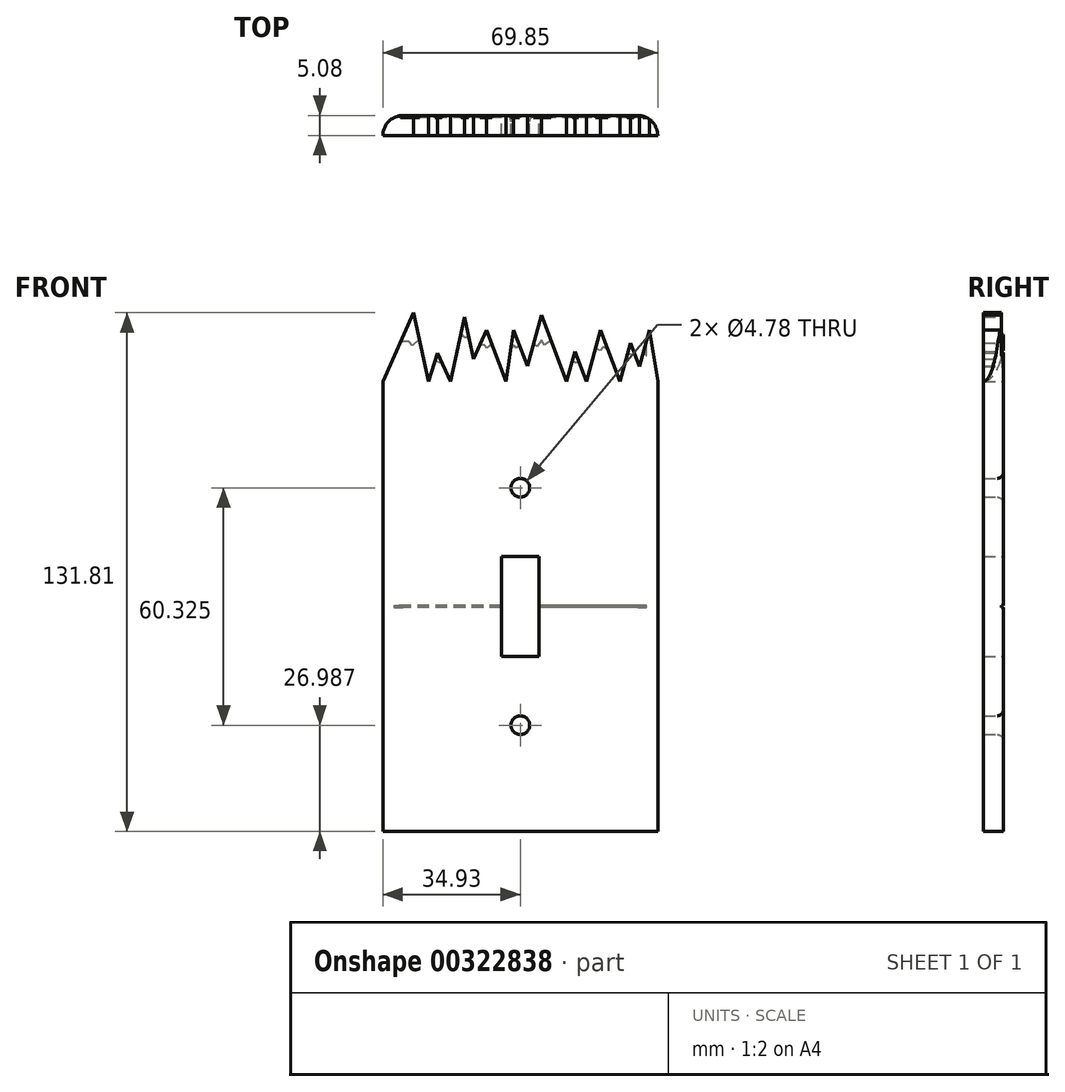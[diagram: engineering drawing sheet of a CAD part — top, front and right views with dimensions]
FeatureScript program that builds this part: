
annotation { "Feature Type Name" : "Feature", "Feature Type Description" : "" }
export const myFeature = defineFeature(function(context is Context, id is Id, definition is map)
    precondition{}
    {
        {
            var Q0;
            Q0=qCreatedBy(makeId("Front.planeOp"),FACE);
            var sketch = newSketch(context, id + "F0", { "sketchPlane" : qUnion([Q0])});
            skLineSegment(sketch, "E0.bottom", {"start": v(34.92, 57.15) * mm, "end": v(-34.93, 57.15) * mm});
            skLineSegment(sketch, "E0.top", {"start": v(34.93, -57.15) * mm, "end": v(-34.92, -57.15) * mm});
            skLineSegment(sketch, "E0.left", {"start": v(34.92, 57.15) * mm, "end": v(34.93, -57.15) * mm});
            skLineSegment(sketch, "E0.right", {"start": v(-34.93, 57.15) * mm, "end": v(-34.92, -57.15) * mm});
            skPoint(sketch, "E0.middle", {"position": v(0, 0) * mm});
            skLineSegment(sketch, "E1.bottom", {"start": v(4.76, 12.7) * mm, "end": v(-4.76, 12.7) * mm});
            skLineSegment(sketch, "E1.top", {"start": v(4.76, -12.7) * mm, "end": v(-4.76, -12.7) * mm});
            skLineSegment(sketch, "E1.left", {"start": v(4.76, 12.7) * mm, "end": v(4.76, -12.7) * mm});
            skLineSegment(sketch, "E1.right", {"start": v(-4.76, 12.7) * mm, "end": v(-4.76, -12.7) * mm});
            skCircle(sketch, "E2", {"center": v(0, 30.16) * mm, "radius": 2.39 * mm});
            skCircle(sketch, "E3", {"center": v(0, -30.16) * mm, "radius": 2.39 * mm});
            skSolve(sketch);
        }
        {
            var Q0;
            Q0=makeQuery(id+"F0.imprint","IMPRINT",FACE,{"disambiguationData":[TD([[makeQuery(id+"F0.imprint","IMPRINT",EDGE,{"derivedFrom":sQuery(id+"F0.wireOp",EDGE,"E0.bottom")}),1.0]])]});
            var sketch = newSketch(context, id + "F1", { "sketchPlane" : qUnion([Q0])});
            skSolve(sketch);
        }
        {
            var Q0;
            Q0=makeQuery(id+"F1.imprint","IMPRINT",FACE,{"disambiguationData":[TD([[makeQuery(id+"F1.imprint","IMPRINT",EDGE,{"derivedFrom":makeQuery(id+"F0.imprint","IMPRINT",EDGE,{"derivedFrom":sQuery(id+"F0.wireOp",EDGE,"E0.bottom")})}),1.0]])]});
            var sketch = newSketch(context, id + "F2", { "sketchPlane" : qUnion([Q0])});
            skLineSegment(sketch, "E4.0.0", {"start": v(-34.92, -57.15) * mm, "end": v(34.93, -57.15) * mm});
            skLineSegment(sketch, "E4.0.1", {"start": v(34.93, -57.15) * mm, "end": v(34.92, 57.15) * mm});
            skLineSegment(sketch, "E4.0.2", {"start": v(34.92, 57.15) * mm, "end": v(-34.93, 57.15) * mm});
            skLineSegment(sketch, "E4.0.3", {"start": v(-34.93, 57.15) * mm, "end": v(-34.92, -57.15) * mm});
            skLineSegment(sketch, "E5", {"start": v(-34.93, 57.15) * mm, "end": v(-27.12, 74.66) * mm});
            skLineSegment(sketch, "E6", {"start": v(-27.12, 74.66) * mm, "end": v(-23.3, 57.15) * mm});
            skLineSegment(sketch, "E7", {"start": v(-23.3, 57.15) * mm, "end": v(-21, 64.35) * mm});
            skLineSegment(sketch, "E8", {"start": v(-21, 64.35) * mm, "end": v(-17.76, 57.15) * mm});
            skLineSegment(sketch, "E9", {"start": v(-17.76, 57.15) * mm, "end": v(-14.13, 73.52) * mm});
            skLineSegment(sketch, "E10", {"start": v(-14.13, 73.52) * mm, "end": v(-11.84, 62.82) * mm});
            skLineSegment(sketch, "E11", {"start": v(-11.84, 62.82) * mm, "end": v(-8.6, 70.27) * mm});
            skLineSegment(sketch, "E12", {"start": v(-8.6, 70.27) * mm, "end": v(-3.63, 57.15) * mm});
            skLineSegment(sketch, "E13", {"start": v(-3.63, 57.15) * mm, "end": v(-1.72, 70.27) * mm});
            skLineSegment(sketch, "E14", {"start": v(-1.72, 70.27) * mm, "end": v(1.77, 61.05) * mm});
            skLineSegment(sketch, "E15", {"start": v(1.77, 61.05) * mm, "end": v(5.35, 74.1) * mm});
            skLineSegment(sketch, "E16", {"start": v(5.35, 74.1) * mm, "end": v(11.76, 57.15) * mm});
            skLineSegment(sketch, "E17", {"start": v(11.76, 57.15) * mm, "end": v(13.86, 64.8) * mm});
            skLineSegment(sketch, "E18", {"start": v(13.86, 64.8) * mm, "end": v(16.76, 57.15) * mm});
            skLineSegment(sketch, "E19", {"start": v(16.76, 57.15) * mm, "end": v(20.36, 70.27) * mm});
            skLineSegment(sketch, "E20", {"start": v(20.36, 70.27) * mm, "end": v(25.32, 57.15) * mm});
            skLineSegment(sketch, "E21", {"start": v(25.32, 57.15) * mm, "end": v(27.99, 66.87) * mm});
            skLineSegment(sketch, "E22", {"start": v(27.99, 66.87) * mm, "end": v(30.22, 60.98) * mm});
            skLineSegment(sketch, "E23", {"start": v(30.22, 60.98) * mm, "end": v(32.77, 70.27) * mm});
            skLineSegment(sketch, "E24", {"start": v(32.77, 70.27) * mm, "end": v(34.92, 57.15) * mm});
            skLineSegment(sketch, "E25", {"start": v(-29.32, 69.72) * mm, "end": v(-28.13, 67.6) * mm});
            skLineSegment(sketch, "E26", {"start": v(-28.13, 67.6) * mm, "end": v(-27.43, 69.16) * mm});
            skLineSegment(sketch, "E27", {"start": v(-27.43, 69.16) * mm, "end": v(-25.61, 67.76) * mm});
            skLineSegment(sketch, "E28", {"start": v(-22.15, 60.75) * mm, "end": v(-19.85, 61.79) * mm});
            skLineSegment(sketch, "E29", {"start": v(-15.51, 67.28) * mm, "end": v(-13.9, 64.92) * mm});
            skLineSegment(sketch, "E30", {"start": v(-13.9, 64.92) * mm, "end": v(-12.71, 66.9) * mm});
            skLineSegment(sketch, "E31", {"start": v(-10.4, 66.1) * mm, "end": v(-8.65, 63.97) * mm});
            skPoint(sketch, "E31.startSnap0", {"position": v(-14.7, 66.1) * mm});
            skLineSegment(sketch, "E32", {"start": v(-8.65, 63.97) * mm, "end": v(-8.08, 65.28) * mm});
            skLineSegment(sketch, "E33", {"start": v(-8.08, 65.28) * mm, "end": v(-6.43, 64.56) * mm});
            skLineSegment(sketch, "E34", {"start": v(-2.48, 65.04) * mm, "end": v(0.03, 65.98) * mm});
            skPoint(sketch, "E34.endSnap0", {"position": v(0.03, 65.66) * mm});
            skLineSegment(sketch, "E35", {"start": v(3.56, 67.57) * mm, "end": v(4.52, 65.04) * mm});
            skLineSegment(sketch, "E36", {"start": v(4.52, 65.04) * mm, "end": v(5.15, 67.35) * mm});
            skLineSegment(sketch, "E37", {"start": v(5.15, 67.35) * mm, "end": v(6.72, 65.04) * mm});
            skLineSegment(sketch, "E38", {"start": v(6.72, 65.04) * mm, "end": v(8.35, 66.14) * mm});
            skLineSegment(sketch, "E39", {"start": v(18.9, 64.96) * mm, "end": v(19.75, 62.72) * mm});
            skLineSegment(sketch, "E40", {"start": v(19.75, 62.72) * mm, "end": v(21.14, 64.25) * mm});
            skLineSegment(sketch, "E41", {"start": v(21.14, 64.25) * mm, "end": v(23.05, 63.16) * mm});
            skLineSegment(sketch, "E42", {"start": v(26.88, 62.84) * mm, "end": v(27.52, 61.17) * mm});
            skLineSegment(sketch, "E43", {"start": v(27.52, 61.17) * mm, "end": v(27.86, 62.44) * mm});
            skLineSegment(sketch, "E44", {"start": v(27.86, 62.44) * mm, "end": v(29.87, 61.89) * mm});
            skLineSegment(sketch, "E45", {"start": v(31.5, 65.63) * mm, "end": v(33.63, 65.04) * mm});
            skSolve(sketch);
        }
        {
            var Q0;
            Q0=makeQuery(id+"F1.imprint","IMPRINT",FACE,{"disambiguationData":[TD([[makeQuery(id+"F1.imprint","IMPRINT",EDGE,{"derivedFrom":makeQuery(id+"F0.imprint","IMPRINT",EDGE,{"derivedFrom":sQuery(id+"F0.wireOp",EDGE,"E0.bottom")})}),1.0]])]});
            extrude(context, id + "F3", {"entities" : qUnion([Q0]), "depth" : 5.08 * mm});
        }
        {
            var Q0;
            {var subQ0=sQuery(id+"F2.wireOp",EDGE,"E39");Q0=makeQuery(id+"F2.imprint","IMPRINT",FACE,{"disambiguationData":[TD([[makeQuery(id+"F2.imprint","IMPRINT",EDGE,{"derivedFrom":subQ0}),-1.0]])]});}
            var Q1;
            {var subQ4=sQuery(id+"F2.wireOp",EDGE,"E39");Q1=makeQuery(id+"F2.imprint","IMPRINT",FACE,{"disambiguationData":[TD([[makeQuery(id+"F2.imprint","IMPRINT",EDGE,{"derivedFrom":subQ4}),1.0]])]});}
            var Q2;
            {var subQ10=sQuery(id+"F2.wireOp",EDGE,"E42");Q2=makeQuery(id+"F2.imprint","IMPRINT",FACE,{"disambiguationData":[TD([[makeQuery(id+"F2.imprint","IMPRINT",EDGE,{"derivedFrom":subQ10}),-1.0]])]});}
            var Q3;
            {var subQ0=sQuery(id+"F2.wireOp",EDGE,"E42");Q3=makeQuery(id+"F2.imprint","IMPRINT",FACE,{"disambiguationData":[TD([[makeQuery(id+"F2.imprint","IMPRINT",EDGE,{"derivedFrom":subQ0}),1.0]])]});}
            var Q4;
            {var subQ3=sQuery(id+"F2.wireOp",EDGE,"E45");Q4=makeQuery(id+"F2.imprint","IMPRINT",FACE,{"disambiguationData":[TD([[makeQuery(id+"F2.imprint","IMPRINT",EDGE,{"derivedFrom":subQ3}),1.0]])]});}
            var Q5;
            {var subQ0=sQuery(id+"F2.wireOp",EDGE,"E17");Q5=makeQuery(id+"F2.imprint","IMPRINT",FACE,{"disambiguationData":[TD([[makeQuery(id+"F2.imprint","IMPRINT",EDGE,{"derivedFrom":subQ0}),-1.0]])]});}
            var Q6;
            {var subQ7=sQuery(id+"F2.wireOp",EDGE,"E35");Q6=makeQuery(id+"F2.imprint","IMPRINT",FACE,{"disambiguationData":[TD([[makeQuery(id+"F2.imprint","IMPRINT",EDGE,{"derivedFrom":subQ7}),-1.0]])]});}
            var Q7;
            {var subQ0=sQuery(id+"F2.wireOp",EDGE,"E35");Q7=makeQuery(id+"F2.imprint","IMPRINT",FACE,{"disambiguationData":[TD([[makeQuery(id+"F2.imprint","IMPRINT",EDGE,{"derivedFrom":subQ0}),1.0]])]});}
            var Q8;
            {var subQ0=sQuery(id+"F2.wireOp",EDGE,"E14");var subQ1=sQuery(id+"F2.wireOp",EDGE,"E13");var subQ2=makeQuery(id+"F2.imprint","INTERSECT",VERTEX,{"derivedFrom":[subQ1,subQ0]});Q8=makeQuery(id+"F2.imprint","IMPRINT",FACE,{"disambiguationData":[TD([[makeQuery(id+"F2.imprint","IMPRINT",EDGE,{"disambiguationData":[TD([[subQ2,1.0]])],"derivedFrom":subQ1}),-1.0]])]});}
            var Q9;
            {var subQ11=sQuery(id+"F2.wireOp",EDGE,"E29");Q9=makeQuery(id+"F2.imprint","IMPRINT",FACE,{"disambiguationData":[TD([[makeQuery(id+"F2.imprint","IMPRINT",EDGE,{"derivedFrom":subQ11}),-1.0]])]});}
            var Q10;
            {var subQ0=sQuery(id+"F2.wireOp",EDGE,"E31");Q10=makeQuery(id+"F2.imprint","IMPRINT",FACE,{"disambiguationData":[TD([[makeQuery(id+"F2.imprint","IMPRINT",EDGE,{"derivedFrom":subQ0}),1.0]])]});}
            var Q11;
            {var subQ3=sQuery(id+"F2.wireOp",EDGE,"E29");Q11=makeQuery(id+"F2.imprint","IMPRINT",FACE,{"disambiguationData":[TD([[makeQuery(id+"F2.imprint","IMPRINT",EDGE,{"derivedFrom":subQ3}),1.0]])]});}
            var Q12;
            {var subQ3=sQuery(id+"F2.wireOp",EDGE,"E28");Q12=makeQuery(id+"F2.imprint","IMPRINT",FACE,{"disambiguationData":[TD([[makeQuery(id+"F2.imprint","IMPRINT",EDGE,{"derivedFrom":subQ3}),-1.0]])]});}
            var Q13;
            {var subQ0=sQuery(id+"F2.wireOp",EDGE,"E25");Q13=makeQuery(id+"F2.imprint","IMPRINT",FACE,{"disambiguationData":[TD([[makeQuery(id+"F2.imprint","IMPRINT",EDGE,{"derivedFrom":subQ0}),-1.0]])]});}
            var Q14;
            {var subQ0=sQuery(id+"F2.wireOp",EDGE,"E25");Q14=makeQuery(id+"F2.imprint","IMPRINT",FACE,{"disambiguationData":[TD([[makeQuery(id+"F2.imprint","IMPRINT",EDGE,{"derivedFrom":subQ0}),1.0]])]});}
            var Q15;
            {var subQ3=sQuery(id+"F2.wireOp",EDGE,"E28");Q15=makeQuery(id+"F2.imprint","IMPRINT",FACE,{"disambiguationData":[TD([[makeQuery(id+"F2.imprint","IMPRINT",EDGE,{"derivedFrom":subQ3}),1.0]])]});}
            extrude(context, id + "F4", {"entities" : qUnion([Q0, Q1, Q2, Q3, Q4, Q5, Q6, Q7, Q8, Q9, Q10, Q11, Q12, Q13, Q14, Q15]), "operationType" : NewBodyOperationType.ADD, "depth" : 5.08 * mm});
        }
        {
            var Q0;
            {var subQ0=sQuery(id+"F2.wireOp",EDGE,"E4.0.2");Q0=makeQuery(id+"F4.boolean.opBoolean","MERGE",FACE,{"derivedFrom":[makeQuery(id+"F3.opExtrude","CAP_FACE",FACE,{"disambiguationData":[OSD([sQuery(id+"F0.wireOp",EDGE,"E0.bottom"),sQuery(id+"F0.wireOp",EDGE,"E0.top"),sQuery(id+"F0.wireOp",EDGE,"E0.left"),sQuery(id+"F0.wireOp",EDGE,"E0.right"),sQuery(id+"F0.wireOp",EDGE,"E1.bottom"),sQuery(id+"F0.wireOp",EDGE,"E1.top"),sQuery(id+"F0.wireOp",EDGE,"E1.left"),sQuery(id+"F0.wireOp",EDGE,"E1.right"),sQuery(id+"F0.wireOp",EDGE,"E2"),sQuery(id+"F0.wireOp",EDGE,"E3")])],"isStart":true}),makeQuery(id+"F4.opExtrude","CAP_FACE",FACE,{"disambiguationData":[OSD([sQuery(id+"F2.wireOp",EDGE,"E5"),sQuery(id+"F2.wireOp",EDGE,"E6"),subQ0])],"isStart":true}),makeQuery(id+"F4.opExtrude","CAP_FACE",FACE,{"disambiguationData":[OSD([sQuery(id+"F2.wireOp",EDGE,"E7"),sQuery(id+"F2.wireOp",EDGE,"E8"),subQ0])],"isStart":true}),makeQuery(id+"F4.opExtrude","CAP_FACE",FACE,{"disambiguationData":[OSD([sQuery(id+"F2.wireOp",EDGE,"E9"),sQuery(id+"F2.wireOp",EDGE,"E10"),sQuery(id+"F2.wireOp",EDGE,"E11"),sQuery(id+"F2.wireOp",EDGE,"E12"),subQ0])],"isStart":true}),makeQuery(id+"F4.opExtrude","CAP_FACE",FACE,{"disambiguationData":[OSD([sQuery(id+"F2.wireOp",EDGE,"E13"),sQuery(id+"F2.wireOp",EDGE,"E14"),sQuery(id+"F2.wireOp",EDGE,"E15"),sQuery(id+"F2.wireOp",EDGE,"E16"),subQ0])],"isStart":true}),makeQuery(id+"F4.opExtrude","CAP_FACE",FACE,{"disambiguationData":[OSD([sQuery(id+"F2.wireOp",EDGE,"E17"),sQuery(id+"F2.wireOp",EDGE,"E18"),subQ0])],"isStart":true}),makeQuery(id+"F4.opExtrude","CAP_FACE",FACE,{"disambiguationData":[OSD([sQuery(id+"F2.wireOp",EDGE,"E19"),sQuery(id+"F2.wireOp",EDGE,"E20"),subQ0])],"isStart":true}),makeQuery(id+"F4.opExtrude","CAP_FACE",FACE,{"disambiguationData":[OSD([sQuery(id+"F2.wireOp",EDGE,"E21"),sQuery(id+"F2.wireOp",EDGE,"E22"),sQuery(id+"F2.wireOp",EDGE,"E23"),sQuery(id+"F2.wireOp",EDGE,"E24"),subQ0])],"isStart":true})]});}
            var sketch = newSketch(context, id + "F5", { "sketchPlane" : qUnion([Q0])});
            skLineSegment(sketch, "E46", {"start": v(-33.59, 65.27) * mm, "end": v(-32.01, 63.77) * mm});
            skLineSegment(sketch, "E47", {"start": v(-32.01, 63.77) * mm, "end": v(-31.21, 64.6) * mm});
            skLineSegment(sketch, "E48", {"start": v(-28.9, 64.47) * mm, "end": v(-28.5, 63.85) * mm});
            skLineSegment(sketch, "E49", {"start": v(-28.5, 63.85) * mm, "end": v(-27.99, 64.17) * mm});
            skLineSegment(sketch, "E50", {"start": v(-27.99, 64.17) * mm, "end": v(-27.15, 63.81) * mm});
            skLineSegment(sketch, "E51", {"start": v(-22.32, 65.07) * mm, "end": v(-21.16, 66.1) * mm});
            skLineSegment(sketch, "E52", {"start": v(-21.16, 66.1) * mm, "end": v(-20.2, 65.02) * mm});
            skLineSegment(sketch, "E53", {"start": v(-20.2, 65.02) * mm, "end": v(-19.1, 65.7) * mm});
            skLineSegment(sketch, "E54", {"start": v(-14.84, 62.2) * mm, "end": v(-13.97, 61.87) * mm});
            skLineSegment(sketch, "E55", {"start": v(-13.97, 61.87) * mm, "end": v(-13.23, 62.5) * mm});
            skLineSegment(sketch, "E56", {"start": v(-7.83, 67.54) * mm, "end": v(-6.13, 66.44) * mm});
            skLineSegment(sketch, "E57", {"start": v(-6.13, 66.44) * mm, "end": v(-5.35, 67.64) * mm});
            skLineSegment(sketch, "E58", {"start": v(-5.35, 67.64) * mm, "end": v(-4.25, 65.99) * mm});
            skLineSegment(sketch, "E59", {"start": v(-4.25, 65.99) * mm, "end": v(-3.3, 66.62) * mm});
            skLineSegment(sketch, "E60", {"start": v(0.22, 66.3) * mm, "end": v(0.99, 65.66) * mm});
            skPoint(sketch, "E60.endSnap0", {"position": v(-0.03, 65.66) * mm});
            skLineSegment(sketch, "E61", {"start": v(0.99, 65.66) * mm, "end": v(1.48, 66.26) * mm});
            skLineSegment(sketch, "E62", {"start": v(1.48, 66.26) * mm, "end": v(2.42, 65.48) * mm});
            skLineSegment(sketch, "E63", {"start": v(7.22, 66.64) * mm, "end": v(8.5, 65.66) * mm});
            skLineSegment(sketch, "E64", {"start": v(8.5, 65.66) * mm, "end": v(9.08, 66.42) * mm});
            skLineSegment(sketch, "E65", {"start": v(9.08, 66.42) * mm, "end": v(10.27, 66.42) * mm});
            skLineSegment(sketch, "E66", {"start": v(13.18, 69.07) * mm, "end": v(13.92, 68.17) * mm});
            skPoint(sketch, "E66.endSnap0", {"position": v(12.98, 68.17) * mm});
            skLineSegment(sketch, "E67", {"start": v(13.92, 68.17) * mm, "end": v(15.1, 69.14) * mm});
            skLineSegment(sketch, "E68", {"start": v(19.84, 61.76) * mm, "end": v(21.65, 62.34) * mm});
            skLineSegment(sketch, "E69", {"start": v(25.64, 67.9) * mm, "end": v(27.34, 66.26) * mm});
            skLineSegment(sketch, "E70", {"start": v(27.34, 66.26) * mm, "end": v(28.33, 67.29) * mm});
            skLineSegment(sketch, "E71", {"start": v(28.33, 67.29) * mm, "end": v(30.4, 67.29) * mm});
            skSolve(sketch);
        }
        {
            var Q0;
            {var subQ0=sQuery(id+"F5.wireOp",EDGE,"E46");Q0=makeQuery(id+"F5.imprint","IMPRINT",FACE,{"disambiguationData":[TD([[makeQuery(id+"F5.imprint","IMPRINT",EDGE,{"derivedFrom":subQ0}),1.0]])]});}
            var Q1;
            {var subQ4=sQuery(id+"F5.wireOp",EDGE,"E48");Q1=makeQuery(id+"F5.imprint","IMPRINT",FACE,{"disambiguationData":[TD([[makeQuery(id+"F5.imprint","IMPRINT",EDGE,{"derivedFrom":subQ4}),1.0]])]});}
            var Q2;
            {var subQ4=sQuery(id+"F5.wireOp",EDGE,"E51");Q2=makeQuery(id+"F5.imprint","IMPRINT",FACE,{"disambiguationData":[TD([[makeQuery(id+"F5.imprint","IMPRINT",EDGE,{"derivedFrom":subQ4}),1.0]])]});}
            var Q3;
            {var subQ0=sQuery(id+"F5.wireOp",EDGE,"E54");Q3=makeQuery(id+"F5.imprint","IMPRINT",FACE,{"disambiguationData":[TD([[makeQuery(id+"F5.imprint","IMPRINT",EDGE,{"derivedFrom":subQ0}),1.0]])]});}
            var Q4;
            {var subQ4=sQuery(id+"F5.wireOp",EDGE,"E56");Q4=makeQuery(id+"F5.imprint","IMPRINT",FACE,{"disambiguationData":[TD([[makeQuery(id+"F5.imprint","IMPRINT",EDGE,{"derivedFrom":subQ4}),1.0]])]});}
            var Q5;
            {var subQ4=sQuery(id+"F5.wireOp",EDGE,"E60");Q5=makeQuery(id+"F5.imprint","IMPRINT",FACE,{"disambiguationData":[TD([[makeQuery(id+"F5.imprint","IMPRINT",EDGE,{"derivedFrom":subQ4}),1.0]])]});}
            var Q6;
            {var subQ4=sQuery(id+"F5.wireOp",EDGE,"E63");Q6=makeQuery(id+"F5.imprint","IMPRINT",FACE,{"disambiguationData":[TD([[makeQuery(id+"F5.imprint","IMPRINT",EDGE,{"derivedFrom":subQ4}),1.0]])]});}
            var Q7;
            {var subQ0=sQuery(id+"F5.wireOp",EDGE,"E66");Q7=makeQuery(id+"F5.imprint","IMPRINT",FACE,{"disambiguationData":[TD([[makeQuery(id+"F5.imprint","IMPRINT",EDGE,{"derivedFrom":subQ0}),1.0]])]});}
            var Q8;
            {var subQ0=sQuery(id+"F5.wireOp",EDGE,"E68");Q8=makeQuery(id+"F5.imprint","IMPRINT",FACE,{"disambiguationData":[TD([[makeQuery(id+"F5.imprint","IMPRINT",EDGE,{"derivedFrom":subQ0}),1.0]])]});}
            var Q9;
            {var subQ4=sQuery(id+"F5.wireOp",EDGE,"E69");Q9=makeQuery(id+"F5.imprint","IMPRINT",FACE,{"disambiguationData":[TD([[makeQuery(id+"F5.imprint","IMPRINT",EDGE,{"derivedFrom":subQ4}),1.0]])]});}
            extrude(context, id + "F6", {"entities" : qUnion([Q0, Q1, Q2, Q3, Q4, Q5, Q6, Q7, Q8, Q9]), "operationType" : NewBodyOperationType.REMOVE, "oppositeDirection" : true, "depth" : 0.5 * mm});
        }
        {
            var Q0;
            Q0=makeQuery(id+"F1.imprint","IMPRINT",FACE,{"disambiguationData":[TD([[makeQuery(id+"F1.imprint","IMPRINT",EDGE,{"derivedFrom":makeQuery(id+"F0.imprint","IMPRINT",EDGE,{"derivedFrom":sQuery(id+"F0.wireOp",EDGE,"E0.bottom")})}),1.0]])]});
            var sketch = newSketch(context, id + "F7", { "sketchPlane" : qUnion([Q0])});
            skLineSegment(sketch, "E72.0", {"start": v(34.93, 0.25) * mm, "end": v(4.76, 0.25) * mm});
            skLineSegment(sketch, "E73.0", {"start": v(34.93, -0.25) * mm, "end": v(4.76, -0.25) * mm});
            skLineSegment(sketch, "E74.0", {"start": v(-4.76, 0.25) * mm, "end": v(-34.93, 0.25) * mm});
            skLineSegment(sketch, "E75.0", {"start": v(-4.76, -0.25) * mm, "end": v(-34.93, -0.25) * mm});
            skLineSegment(sketch, "E76", {"start": v(4.76, 0.25) * mm, "end": v(4.76, -0.25) * mm});
            skLineSegment(sketch, "E77", {"start": v(34.93, 0.25) * mm, "end": v(34.93, -0.25) * mm});
            skLineSegment(sketch, "E78", {"start": v(-4.76, 0.25) * mm, "end": v(-4.76, -0.25) * mm});
            skLineSegment(sketch, "E79", {"start": v(-34.93, 0.25) * mm, "end": v(-34.93, -0.25) * mm});
            skSolve(sketch);
        }
        {
            var Q0;
            Q0 = qSketchRegion(id + "F7", true);
            extrude(context, id + "F8", {"entities" : qUnion([Q0]), "operationType" : NewBodyOperationType.REMOVE, "depth" : 0.5 * mm});
        }
        {
            var Q0;
            {var subQ1=sQuery(id+"F0.wireOp",EDGE,"E0.right");var subQ2=sQuery(id+"F0.wireOp",EDGE,"E0.top");Q0=makeQuery(id+"F8.boolean.opBoolean","SPLIT",EDGE,{"disambiguationData":[TD([makeQuery(id+"F3.opExtrude","SWEPT_FACE",FACE,{"disambiguationData":[OSD([subQ2])]})])],"derivedFrom":makeQuery(id+"F3.opExtrude","CAP_EDGE",EDGE,{"disambiguationData":[OSD([subQ1])],"isStart":true})});}
            var Q1;
            {var subQ1=sQuery(id+"F0.wireOp",EDGE,"E0.right");var subQ2=sQuery(id+"F2.wireOp",EDGE,"E5");Q1=makeQuery(id+"F8.boolean.opBoolean","SPLIT",EDGE,{"disambiguationData":[TD([makeQuery(id+"F4.opExtrude","SWEPT_FACE",FACE,{"disambiguationData":[OSD([subQ2])]})])],"derivedFrom":makeQuery(id+"F3.opExtrude","CAP_EDGE",EDGE,{"disambiguationData":[OSD([subQ1])],"isStart":true})});}
            var Q2;
            {var subQ1=sQuery(id+"F2.wireOp",EDGE,"E24");var subQ2=sQuery(id+"F0.wireOp",EDGE,"E0.left");Q2=makeQuery(id+"F8.boolean.opBoolean","SPLIT",EDGE,{"disambiguationData":[TD([makeQuery(id+"F4.opExtrude","SWEPT_FACE",FACE,{"disambiguationData":[OSD([subQ1])]})])],"derivedFrom":makeQuery(id+"F3.opExtrude","CAP_EDGE",EDGE,{"disambiguationData":[OSD([subQ2])],"isStart":true})});}
            var Q3;
            {var subQ1=sQuery(id+"F0.wireOp",EDGE,"E0.left");var subQ2=sQuery(id+"F0.wireOp",EDGE,"E0.top");Q3=makeQuery(id+"F8.boolean.opBoolean","SPLIT",EDGE,{"disambiguationData":[TD([makeQuery(id+"F3.opExtrude","SWEPT_FACE",FACE,{"disambiguationData":[OSD([subQ2])]})])],"derivedFrom":makeQuery(id+"F3.opExtrude","CAP_EDGE",EDGE,{"disambiguationData":[OSD([subQ1])],"isStart":true})});}
            fillet(context, id + "F9", {"entities" : qUnion([Q0, Q1, Q2, Q3]), "radius" : 5.08 * mm, "tangentPropagation" : true, "allowEdgeOverflow" : false});
        }
        {
            var Q0;
            Q0=makeQuery(id+"F3.opExtrude","CAP_EDGE",EDGE,{"disambiguationData":[OSD([sQuery(id+"F0.wireOp",EDGE,"E2")])],"isStart":true});
            var Q1;
            Q1=makeQuery(id+"F3.opExtrude","CAP_EDGE",EDGE,{"disambiguationData":[OSD([sQuery(id+"F0.wireOp",EDGE,"E3")])],"isStart":true});
            fillet(context, id + "F10", {"entities" : qUnion([Q0, Q1]), "radius" : 1.52 * mm, "tangentPropagation" : true, "allowEdgeOverflow" : false});
        }
    });
